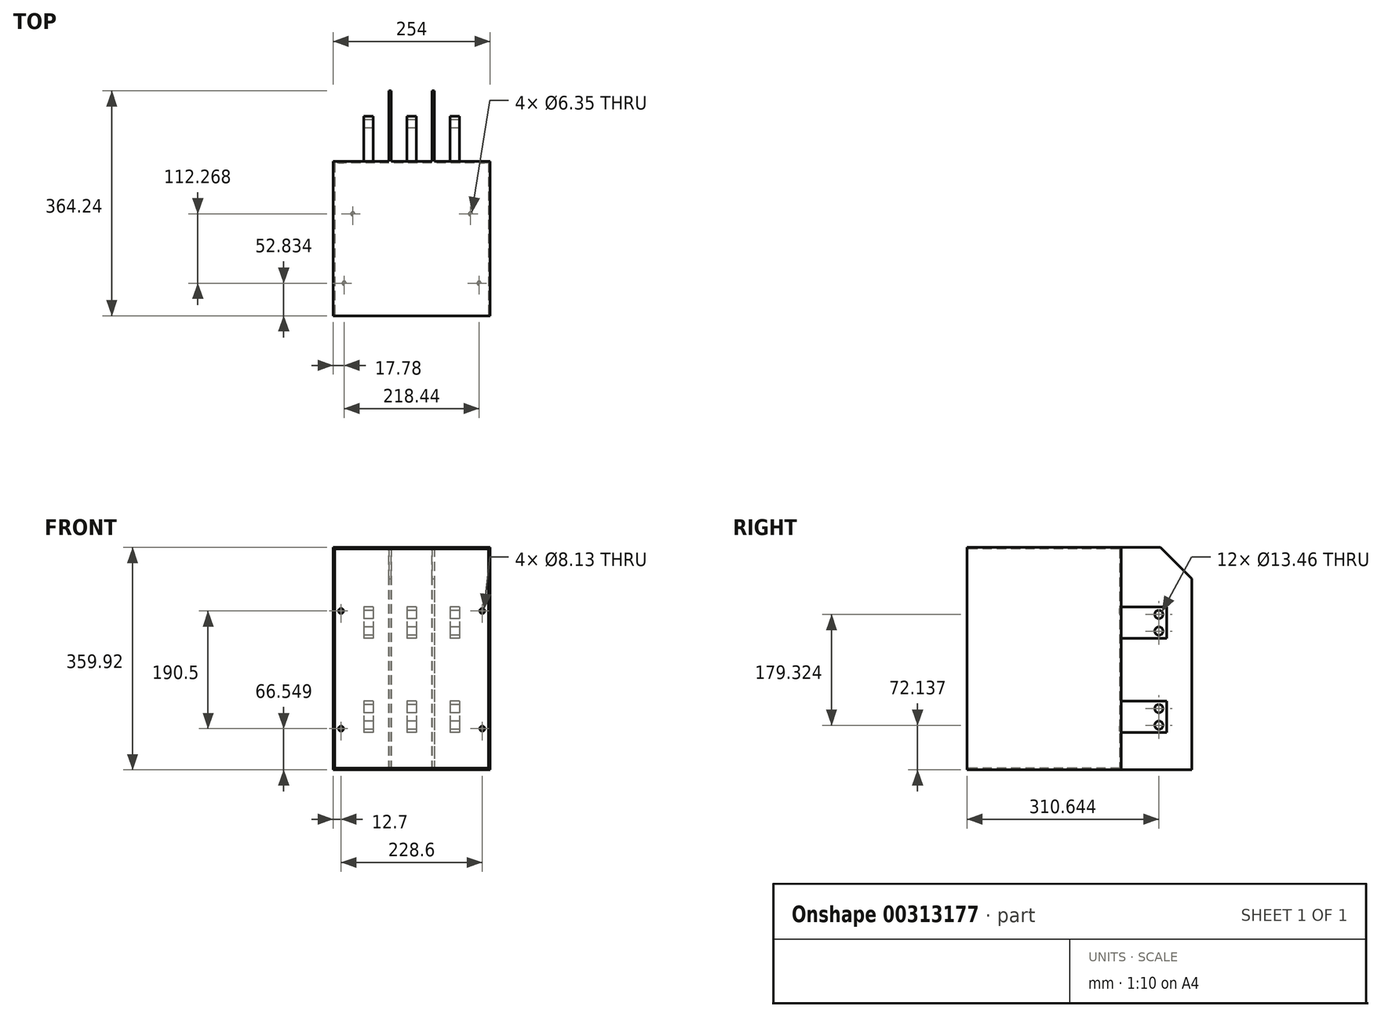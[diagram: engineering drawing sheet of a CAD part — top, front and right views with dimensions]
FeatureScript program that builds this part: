
annotation { "Feature Type Name" : "Feature", "Feature Type Description" : "" }
export const myFeature = defineFeature(function(context is Context, id is Id, definition is map)
    precondition{}
    {
        {
            var Q0;
            Q0=qCreatedBy(makeId("Right.planeOp"),FACE);
            var sketch = newSketch(context, id + "F0", { "sketchPlane" : qUnion([Q0])});
            skLineSegment(sketch, "E0.bottom", {"start": v(124.97, 179.96) * mm, "end": v(-124.97, 179.96) * mm});
            skLineSegment(sketch, "E0.top", {"start": v(124.97, -179.96) * mm, "end": v(-124.97, -179.96) * mm});
            skLineSegment(sketch, "E0.left", {"start": v(124.97, 179.96) * mm, "end": v(124.97, -179.96) * mm});
            skLineSegment(sketch, "E0.right", {"start": v(-124.97, 179.96) * mm, "end": v(-124.97, -179.96) * mm});
            skPoint(sketch, "E0.middle", {"position": v(0, 0) * mm});
            skSolve(sketch);
        }
        {
            var Q0;
            Q0=makeQuery(id+"F0.imprint","IMPRINT",FACE,{"disambiguationData":[TD([[makeQuery(id+"F0.imprint","IMPRINT",EDGE,{"derivedFrom":sQuery(id+"F0.wireOp",EDGE,"E0.bottom")}),1.0]])]});
            extrude(context, id + "F1", {"entities" : qUnion([Q0]), "endBound" : BoundingType.SYMMETRIC, "depth" : 254 * mm});
        }
        {
            var Q0;
            Q0=makeQuery(id+"F1.opExtrude","SWEPT_FACE",FACE,{"disambiguationData":[OSD([sQuery(id+"F0.wireOp",EDGE,"E0.right")])]});
            shell(context, id + "F2", {"entities" : qUnion([Q0]), "thickness" : 2.54 * mm});
        }
        {
            var Q0;
            Q0=makeQuery(id+"F1.opExtrude","SWEPT_FACE",FACE,{"disambiguationData":[OSD([sQuery(id+"F0.wireOp",EDGE,"E0.left")])]});
            var sketch = newSketch(context, id + "F3", { "sketchPlane" : qUnion([Q0])});
            skLineSegment(sketch, "E1.bottom", {"start": v(62.36, -68.96) * mm, "end": v(77.34, -68.96) * mm});
            skLineSegment(sketch, "E1.top", {"start": v(62.36, -119.76) * mm, "end": v(77.34, -119.76) * mm});
            skLineSegment(sketch, "E1.left", {"start": v(62.36, -68.96) * mm, "end": v(62.36, -119.76) * mm});
            skLineSegment(sketch, "E1.right", {"start": v(77.34, -68.96) * mm, "end": v(77.34, -119.76) * mm});
            skPoint(sketch, "E1.middle", {"position": v(69.85, -94.36) * mm});
            skLineSegment(sketch, "E2.0.1.0", {"start": v(77.34, 83.44) * mm, "end": v(77.34, 32.64) * mm});
            skPoint(sketch, "E2.0.1.1", {"position": v(69.85, 58.04) * mm});
            skLineSegment(sketch, "E2.0.1.2", {"start": v(62.36, 83.44) * mm, "end": v(77.34, 83.44) * mm});
            skLineSegment(sketch, "E2.0.1.3", {"start": v(62.36, 83.44) * mm, "end": v(62.36, 32.64) * mm});
            skLineSegment(sketch, "E2.0.1.4", {"start": v(62.36, 32.64) * mm, "end": v(77.34, 32.64) * mm});
            skLineSegment(sketch, "E2.1.0.0", {"start": v(7.5, -68.96) * mm, "end": v(7.5, -119.76) * mm});
            skPoint(sketch, "E2.1.0.1", {"position": v(0, -94.36) * mm});
            skLineSegment(sketch, "E2.1.0.2", {"start": v(-7.5, -68.96) * mm, "end": v(7.5, -68.96) * mm});
            skLineSegment(sketch, "E2.1.0.3", {"start": v(-7.5, -68.96) * mm, "end": v(-7.5, -119.76) * mm});
            skLineSegment(sketch, "E2.1.0.4", {"start": v(-7.5, -119.76) * mm, "end": v(7.5, -119.76) * mm});
            skLineSegment(sketch, "E2.1.1.0", {"start": v(7.5, 83.44) * mm, "end": v(7.5, 32.64) * mm});
            skPoint(sketch, "E2.1.1.1", {"position": v(0, 58.04) * mm});
            skLineSegment(sketch, "E2.1.1.2", {"start": v(-7.5, 83.44) * mm, "end": v(7.5, 83.44) * mm});
            skLineSegment(sketch, "E2.1.1.3", {"start": v(-7.5, 83.44) * mm, "end": v(-7.5, 32.64) * mm});
            skLineSegment(sketch, "E2.1.1.4", {"start": v(-7.5, 32.64) * mm, "end": v(7.5, 32.64) * mm});
            skLineSegment(sketch, "E2.2.0.0", {"start": v(-62.36, -68.96) * mm, "end": v(-62.36, -119.76) * mm});
            skPoint(sketch, "E2.2.0.1", {"position": v(-69.85, -94.36) * mm});
            skLineSegment(sketch, "E2.2.0.2", {"start": v(-77.34, -68.96) * mm, "end": v(-62.36, -68.96) * mm});
            skLineSegment(sketch, "E2.2.0.3", {"start": v(-77.34, -68.96) * mm, "end": v(-77.34, -119.76) * mm});
            skLineSegment(sketch, "E2.2.0.4", {"start": v(-77.34, -119.76) * mm, "end": v(-62.36, -119.76) * mm});
            skLineSegment(sketch, "E2.2.1.0", {"start": v(-62.36, 83.44) * mm, "end": v(-62.36, 32.64) * mm});
            skPoint(sketch, "E2.2.1.1", {"position": v(-69.85, 58.04) * mm});
            skLineSegment(sketch, "E2.2.1.2", {"start": v(-77.34, 83.44) * mm, "end": v(-62.36, 83.44) * mm});
            skLineSegment(sketch, "E2.2.1.3", {"start": v(-77.34, 83.44) * mm, "end": v(-77.34, 32.64) * mm});
            skLineSegment(sketch, "E2.2.1.4", {"start": v(-77.34, 32.64) * mm, "end": v(-62.36, 32.64) * mm});
            skLineSegment(sketch, "E2.direction1", {"start": v(62.36, -119.76) * mm, "end": v(-7.5, -119.76) * mm, "construction": true});
            skLineSegment(sketch, "E2.direction2", {"start": v(62.36, -119.76) * mm, "end": v(62.36, 32.64) * mm, "construction": true});
            skSolve(sketch);
        }
        {
            var Q0;
            Q0 = qSketchRegion(id + "F3", true);
            extrude(context, id + "F4", {"entities" : qUnion([Q0]), "operationType" : NewBodyOperationType.ADD, "depth" : 73.15 * mm});
        }
        {
            var Q0;
            Q0=qCreatedBy(makeId("Right.planeOp"),FACE);
            var sketch = newSketch(context, id + "F5", { "sketchPlane" : qUnion([Q0])});
            skCircle(sketch, "E3", {"center": v(185.67, 71.5) * mm, "radius": 6.73 * mm});
            skCircle(sketch, "E4", {"center": v(185.67, 44.58) * mm, "radius": 6.73 * mm});
            skCircle(sketch, "E5", {"center": v(185.67, -80.9) * mm, "radius": 6.73 * mm});
            skCircle(sketch, "E6", {"center": v(185.67, -107.82) * mm, "radius": 6.73 * mm});
            skLineSegment(sketch, "E7", {"start": v(185.67, 71.5) * mm, "end": v(185.67, 44.58) * mm, "construction": true});
            skLineSegment(sketch, "E8", {"start": v(185.67, -80.9) * mm, "end": v(185.67, -107.82) * mm, "construction": true});
            skPoint(sketch, "E9", {"position": v(185.67, 58.04) * mm});
            skPoint(sketch, "E10", {"position": v(185.67, -94.36) * mm});
            skSolve(sketch);
        }
        {
            var Q0;
            Q0 = qSketchRegion(id + "F5", true);
            extrude(context, id + "F6", {"entities" : qUnion([Q0]), "operationType" : NewBodyOperationType.REMOVE, "endBound" : BoundingType.THROUGH_ALL, "depth" : 25.4 * mm, "hasSecondDirection" : true, "secondDirectionBound" : SecondDirectionBoundingType.THROUGH_ALL, "secondDirectionOppositeDirection" : true, "secondDirectionDepth" : 25.4 * mm});
        }
        {
            var Q0;
            Q0=makeQuery(id+"F1.opExtrude","SWEPT_FACE",FACE,{"disambiguationData":[OSD([sQuery(id+"F0.wireOp",EDGE,"E0.top")])]});
            var sketch = newSketch(context, id + "F7", { "sketchPlane" : qUnion([Q0])});
            skCircle(sketch, "E11", {"center": v(-109.22, 72.14) * mm, "radius": 3.18 * mm});
            skCircle(sketch, "E12", {"center": v(109.22, 72.14) * mm, "radius": 3.18 * mm});
            skCircle(sketch, "E13", {"center": v(95.25, -40.13) * mm, "radius": 3.18 * mm});
            skCircle(sketch, "E14", {"center": v(-95.25, -40.13) * mm, "radius": 3.18 * mm});
            skSolve(sketch);
        }
        {
            var Q0;
            Q0 = qSketchRegion(id + "F7", true);
            extrude(context, id + "F8", {"entities" : qUnion([Q0]), "operationType" : NewBodyOperationType.REMOVE, "endBound" : BoundingType.UP_TO_NEXT, "oppositeDirection" : true, "depth" : 25.4 * mm});
        }
        {
            var Q0;
            Q0=makeQuery(id+"F2.opShell","OFFSET_FACE",FACE,{"disambiguationData":[OSD([sQuery(id+"F0.wireOp",EDGE,"E0.left")])]});
            var sketch = newSketch(context, id + "F9", { "sketchPlane" : qUnion([Q0])});
            skCircle(sketch, "E15", {"center": v(-114.3, 77.09) * mm, "radius": 4.06 * mm});
            skCircle(sketch, "E16", {"center": v(114.3, 77.09) * mm, "radius": 4.06 * mm});
            skCircle(sketch, "E17", {"center": v(114.3, -113.41) * mm, "radius": 4.06 * mm});
            skCircle(sketch, "E18", {"center": v(-114.3, -113.41) * mm, "radius": 4.06 * mm});
            skSolve(sketch);
        }
        {
            var Q0;
            Q0 = qSketchRegion(id + "F9", true);
            extrude(context, id + "F10", {"entities" : qUnion([Q0]), "operationType" : NewBodyOperationType.REMOVE, "endBound" : BoundingType.THROUGH_ALL, "oppositeDirection" : true, "depth" : 25.4 * mm});
        }
        {
            var Q0;
            Q0=makeQuery(id+"F1.opExtrude","SWEPT_FACE",FACE,{"disambiguationData":[OSD([sQuery(id+"F0.wireOp",EDGE,"E0.left")])]});
            var sketch = newSketch(context, id + "F11", { "sketchPlane" : qUnion([Q0])});
            skLineSegment(sketch, "E19.bottom", {"start": v(-33.02, 179.96) * mm, "end": v(-36.83, 179.96) * mm});
            skLineSegment(sketch, "E19.top", {"start": v(-33.02, -179.96) * mm, "end": v(-36.83, -179.96) * mm});
            skLineSegment(sketch, "E19.left", {"start": v(-33.02, 179.96) * mm, "end": v(-33.02, -179.96) * mm});
            skLineSegment(sketch, "E19.right", {"start": v(-36.83, 179.96) * mm, "end": v(-36.83, -179.96) * mm});
            skPoint(sketch, "E19.middle", {"position": v(-34.92, 0) * mm});
            skPoint(sketch, "E19.middle.positionSnap0", {"position": v(-127, 0) * mm});
            skPoint(sketch, "E19.centerSnap0", {"position": v(-127, 0) * mm});
            skLineSegment(sketch, "E20.bottom", {"start": v(36.83, 179.96) * mm, "end": v(33.02, 179.96) * mm});
            skLineSegment(sketch, "E20.top", {"start": v(36.83, -179.96) * mm, "end": v(33.02, -179.96) * mm});
            skLineSegment(sketch, "E20.left", {"start": v(36.83, 179.96) * mm, "end": v(36.83, -179.96) * mm});
            skLineSegment(sketch, "E20.right", {"start": v(33.02, 179.96) * mm, "end": v(33.02, -179.96) * mm});
            skPoint(sketch, "E20.middle", {"position": v(34.93, 0) * mm});
            skLineSegment(sketch, "E21", {"start": v(-62.36, 58.04) * mm, "end": v(-7.5, 58.04) * mm, "construction": true});
            skPoint(sketch, "E22", {"position": v(-34.92, 58.04) * mm});
            skLineSegment(sketch, "E23", {"start": v(7.5, 58.04) * mm, "end": v(62.36, 58.04) * mm, "construction": true});
            skPoint(sketch, "E24", {"position": v(34.93, 58.04) * mm});
            skSolve(sketch);
        }
        {
            var Q0;
            Q0 = qSketchRegion(id + "F11", true);
            extrude(context, id + "F12", {"entities" : qUnion([Q0]), "operationType" : NewBodyOperationType.ADD, "depth" : 139.7 * mm});
        }
        {
            var Q0;
            Q0=makeQuery(id+"F12.opExtrude","SWEPT_FACE",FACE,{"disambiguationData":[OSD([sQuery(id+"F11.wireOp",EDGE,"E19.right")])]});
            var sketch = newSketch(context, id + "F13", { "sketchPlane" : qUnion([Q0])});
            skLineSegment(sketch, "E25", {"start": v(264.67, 179.96) * mm, "end": v(188.47, 179.96) * mm});
            skLineSegment(sketch, "E26", {"start": v(188.47, 179.96) * mm, "end": v(239.27, 129.16) * mm});
            skLineSegment(sketch, "E27", {"start": v(264.67, 103.76) * mm, "end": v(264.67, 179.96) * mm});
            skLineSegment(sketch, "E28", {"start": v(239.27, 129.16) * mm, "end": v(239.27, -179.96) * mm});
            skLineSegment(sketch, "E29", {"start": v(239.27, -179.96) * mm, "end": v(264.67, -179.96) * mm});
            skLineSegment(sketch, "E30", {"start": v(264.67, -179.96) * mm, "end": v(264.67, 103.76) * mm});
            skSolve(sketch);
        }
        {
            var Q0;
            Q0 = qSketchRegion(id + "F13", true);
            extrude(context, id + "F14", {"entities" : qUnion([Q0]), "operationType" : NewBodyOperationType.REMOVE, "endBound" : BoundingType.THROUGH_ALL, "oppositeDirection" : true, "depth" : 25.4 * mm});
        }
    });
